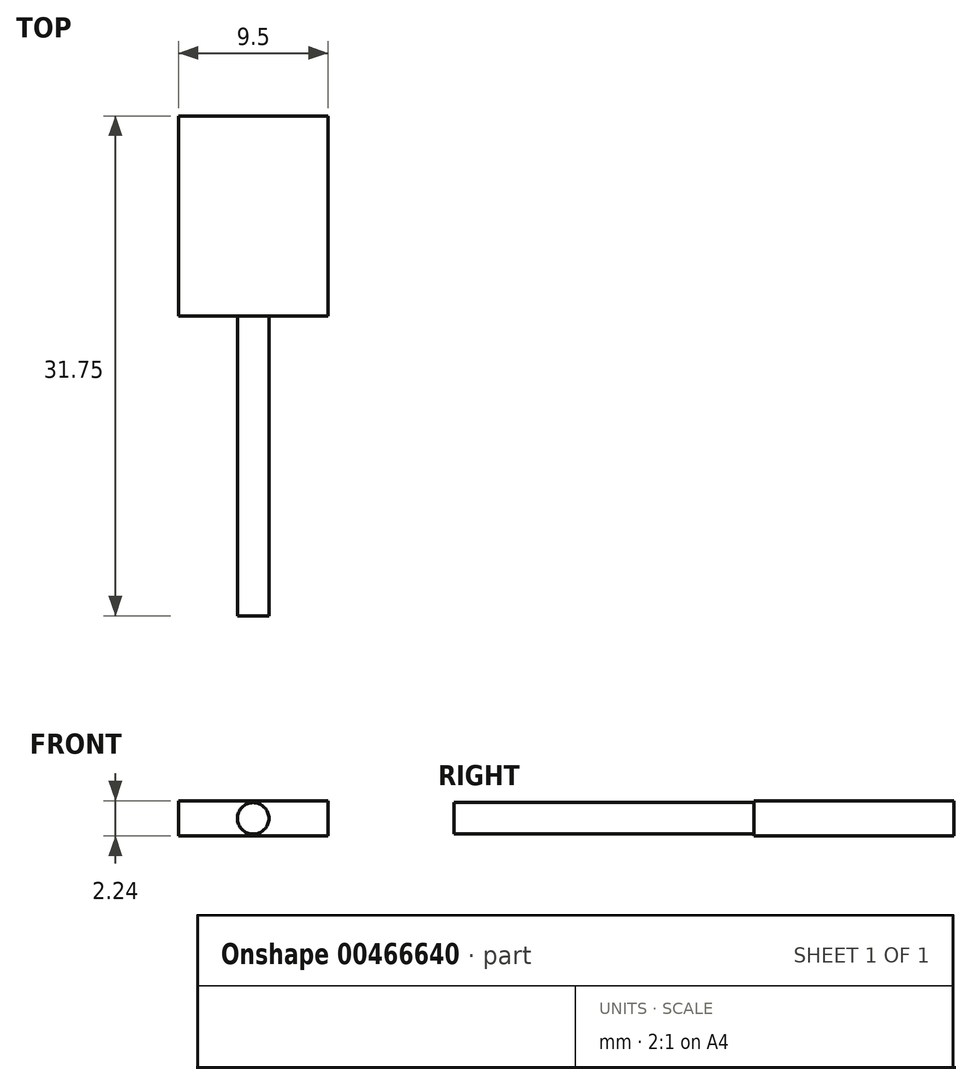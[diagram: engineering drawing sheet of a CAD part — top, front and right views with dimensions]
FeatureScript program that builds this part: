
annotation { "Feature Type Name" : "Feature", "Feature Type Description" : "" }
export const myFeature = defineFeature(function(context is Context, id is Id, definition is map)
    precondition{}
    {
        {
            var Q0;
            Q0=qCreatedBy(makeId("Front.planeOp"),FACE);
            var sketch = newSketch(context, id + "F0", { "sketchPlane" : qUnion([Q0])});
            skCircle(sketch, "E0", {"center": v(0, 0) * mm, "radius": 1 * mm});
            skSolve(sketch);
        }
        {
            var Q0;
            Q0 = qSketchRegion(id + "F0", true);
            var Q1;
            Q1=makeQuery(id+"F0.imprint","IMPRINT",FACE,{"disambiguationData":[TD([[makeQuery(id+"F0.imprint","IMPRINT",EDGE,{"derivedFrom":sQuery(id+"F0.wireOp",EDGE,"E0")}),1.0]])]});
            extrude(context, id + "F1", {"entities" : qUnion([Q0, Q1]), "depth" : 19.05 * mm});
        }
        {
            var Q0;
            Q0=makeQuery(id+"F1.opExtrude","CAP_FACE",FACE,{"disambiguationData":[OSD([sQuery(id+"F0.wireOp",EDGE,"E0")])],"isStart":true});
            var sketch = newSketch(context, id + "F2", { "sketchPlane" : qUnion([Q0])});
            skLineSegment(sketch, "E1.bottom", {"start": v(-4.75, 1.13) * mm, "end": v(4.75, 1.13) * mm});
            skLineSegment(sketch, "E1.top", {"start": v(-4.75, -1.13) * mm, "end": v(4.75, -1.13) * mm});
            skLineSegment(sketch, "E1.left", {"start": v(-4.75, 1.13) * mm, "end": v(-4.75, -1.13) * mm});
            skLineSegment(sketch, "E1.right", {"start": v(4.75, 1.13) * mm, "end": v(4.75, -1.13) * mm});
            skPoint(sketch, "E1.middle", {"position": v(0, 0) * mm});
            skSolve(sketch);
        }
        {
            var Q0;
            Q0 = qSketchRegion(id + "F2", true);
            extrude(context, id + "F3", {"entities" : qUnion([Q0]), "operationType" : NewBodyOperationType.ADD, "depth" : 12.7 * mm});
        }
    });
